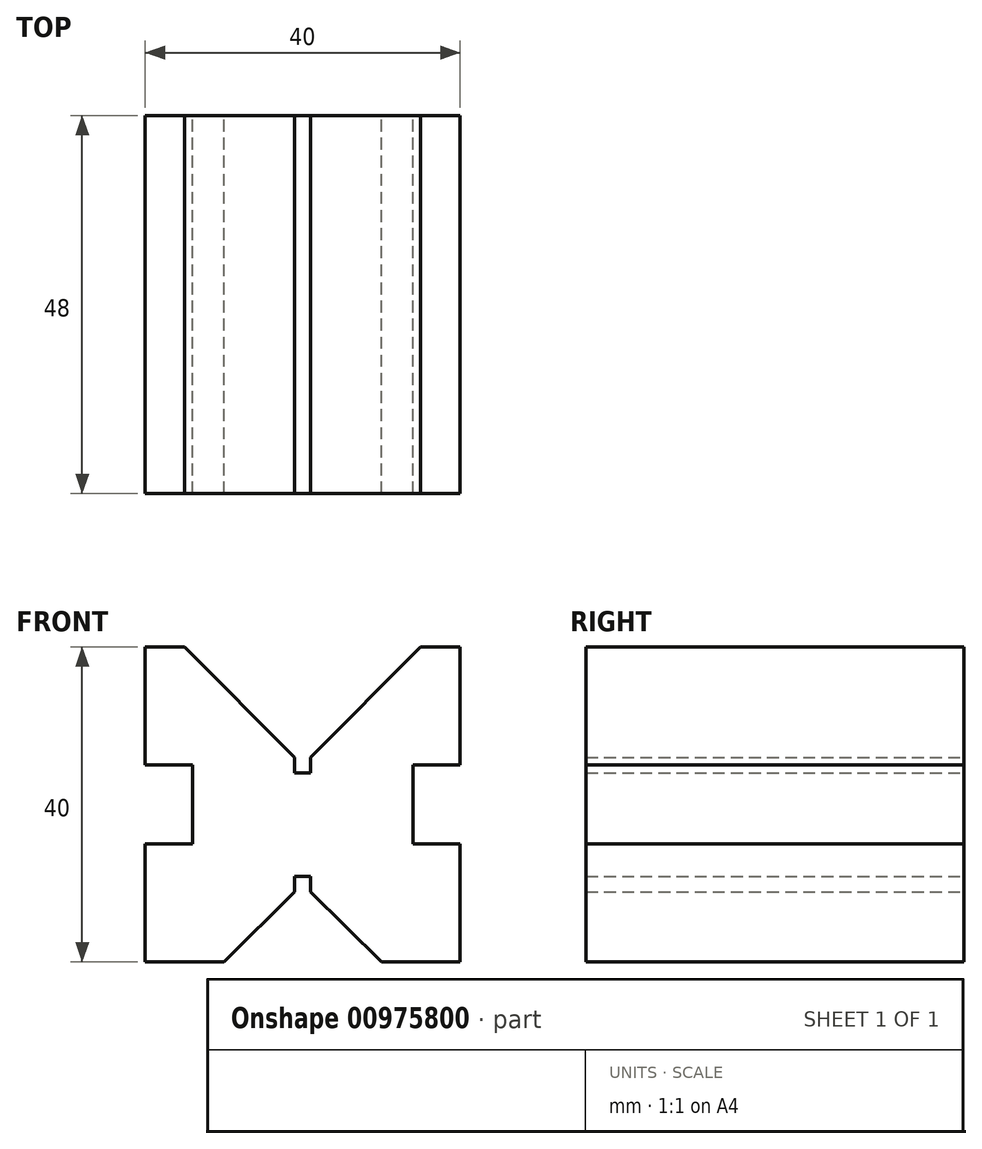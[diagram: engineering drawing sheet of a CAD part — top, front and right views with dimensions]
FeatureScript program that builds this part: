
annotation { "Feature Type Name" : "Feature", "Feature Type Description" : "" }
export const myFeature = defineFeature(function(context is Context, id is Id, definition is map)
    precondition{}
    {
        {
            var Q0;
            Q0=qCreatedBy(makeId("Front.planeOp"),FACE);
            var sketch = newSketch(context, id + "F0", { "sketchPlane" : qUnion([Q0])});
            skLineSegment(sketch, "E0", {"start": v(0, 0) * mm, "end": v(10, 0) * mm});
            skLineSegment(sketch, "E1", {"start": v(0, 0) * mm, "end": v(0, 15) * mm});
            skLineSegment(sketch, "E2", {"start": v(0, 15) * mm, "end": v(6, 15) * mm});
            skLineSegment(sketch, "E3", {"start": v(6, 15) * mm, "end": v(6, 25) * mm});
            skLineSegment(sketch, "E4", {"start": v(6, 25) * mm, "end": v(0, 25) * mm});
            skLineSegment(sketch, "E5", {"start": v(0, 25) * mm, "end": v(0, 40) * mm});
            skLineSegment(sketch, "E6", {"start": v(0, 40) * mm, "end": v(5, 40) * mm});
            skLineSegment(sketch, "E7", {"start": v(35, 40) * mm, "end": v(40, 40) * mm});
            skLineSegment(sketch, "E8", {"start": v(40, 40) * mm, "end": v(40, 25) * mm});
            skLineSegment(sketch, "E9", {"start": v(40, 25) * mm, "end": v(34, 25) * mm});
            skLineSegment(sketch, "E10", {"start": v(34, 25) * mm, "end": v(34, 15) * mm});
            skLineSegment(sketch, "E11", {"start": v(34, 15) * mm, "end": v(40, 15) * mm});
            skLineSegment(sketch, "E12", {"start": v(40, 0) * mm, "end": v(30, 0) * mm});
            skLineSegment(sketch, "E13", {"start": v(21, 10.87) * mm, "end": v(19, 10.87) * mm});
            skLineSegment(sketch, "E14", {"start": v(21, 24) * mm, "end": v(19, 24) * mm});
            skLineSegment(sketch, "E15", {"start": v(19, 10.87) * mm, "end": v(19, 8.87) * mm});
            skLineSegment(sketch, "E16", {"start": v(21, 10.87) * mm, "end": v(21, 8.87) * mm});
            skLineSegment(sketch, "E17", {"start": v(21, 8.87) * mm, "end": v(30, 0) * mm});
            skLineSegment(sketch, "E18", {"start": v(19, 8.87) * mm, "end": v(10, 0) * mm});
            skLineSegment(sketch, "E19", {"start": v(19, 24) * mm, "end": v(19, 26) * mm});
            skLineSegment(sketch, "E20", {"start": v(21, 24) * mm, "end": v(21, 26) * mm});
            skLineSegment(sketch, "E21", {"start": v(35, 40) * mm, "end": v(21, 26) * mm});
            skLineSegment(sketch, "E22", {"start": v(19, 26) * mm, "end": v(5, 40) * mm});
            skLineSegment(sketch, "E23", {"start": v(40, 15) * mm, "end": v(40, 0) * mm});
            skSolve(sketch);
        }
        {
            var Q0;
            Q0=makeQuery(id+"F0.imprint","IMPRINT",FACE,{"disambiguationData":[TD([[makeQuery(id+"F0.imprint","IMPRINT",EDGE,{"derivedFrom":sQuery(id+"F0.wireOp",EDGE,"E0")}),1.0]])]});
            extrude(context, id + "F1", {"entities" : qUnion([Q0]), "depth" : 48 * mm, "offsetDistance" : 25 * mm});
        }
    });
